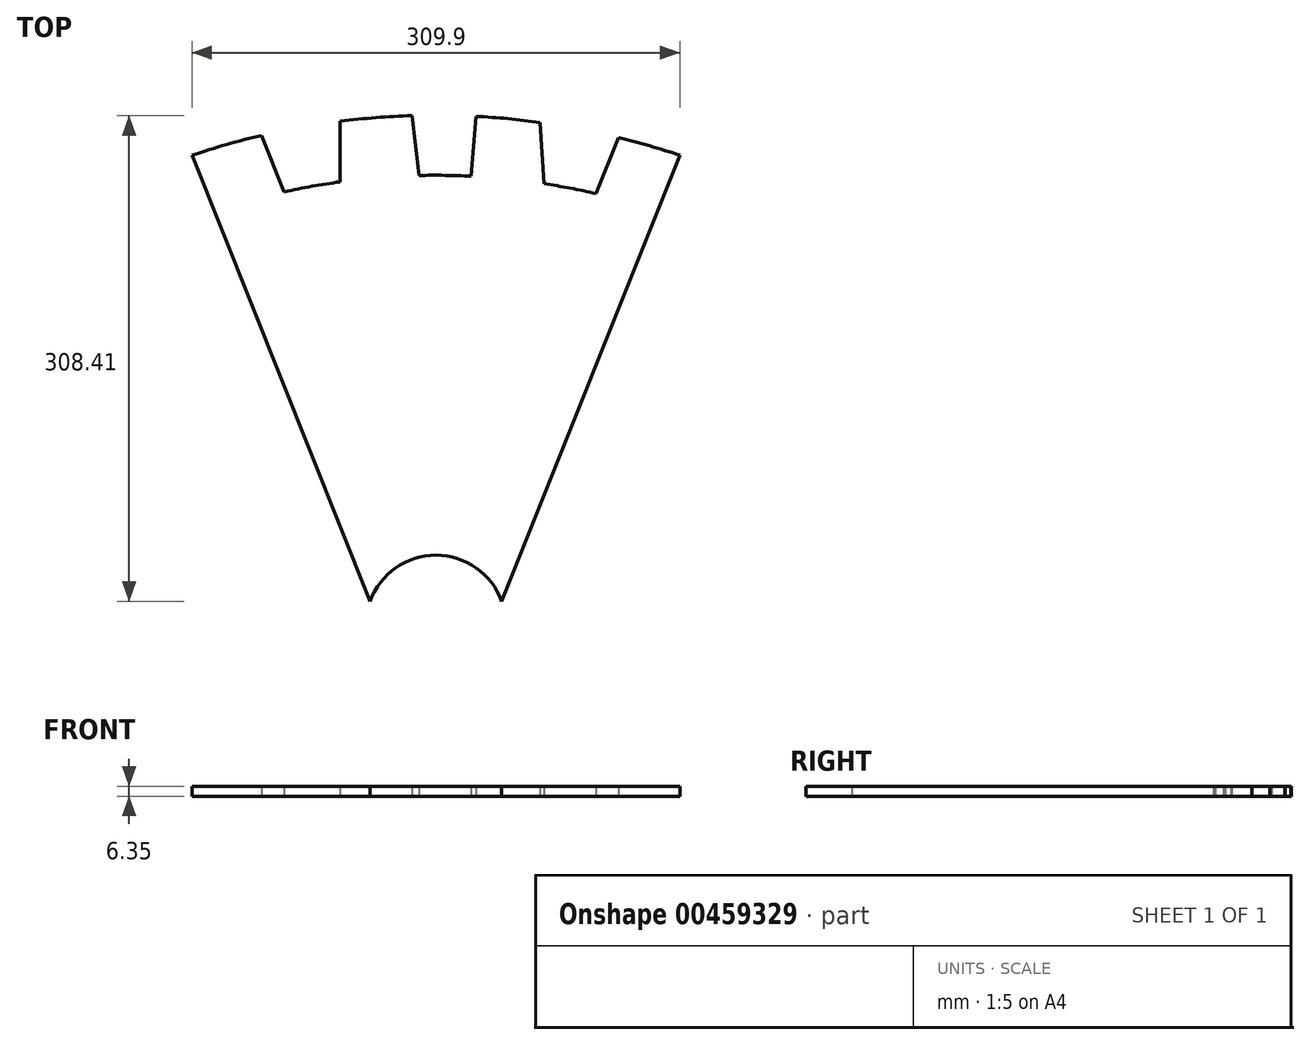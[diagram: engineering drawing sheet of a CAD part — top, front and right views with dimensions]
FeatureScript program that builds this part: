
annotation { "Feature Type Name" : "Feature", "Feature Type Description" : "" }
export const myFeature = defineFeature(function(context is Context, id is Id, definition is map)
    precondition{}
    {
        {
            var Q0;
            Q0=qCreatedBy(makeId("Top.planeOp"),FACE);
            var sketch = newSketch(context, id + "F0", { "sketchPlane" : qUnion([Q0])});
            skCircle(sketch, "E0", {"center": v(0, 0) * mm, "radius": 44.45 * mm});
            skLineSegment(sketch, "E1", {"start": v(0, 0) * mm, "end": v(41.77, 15.2) * mm});
            skLineSegment(sketch, "E2", {"start": v(0, 0) * mm, "end": v(-41.77, 15.2) * mm});
            skLineSegment(sketch, "E3", {"start": v(0, 44.45) * mm, "end": v(0, 323.85) * mm});
            skLineSegment(sketch, "E4", {"start": v(0, 323.85) * mm, "end": v(-165.1, 323.85) * mm});
            skLineSegment(sketch, "E5", {"start": v(0, 323.85) * mm, "end": v(165.1, 323.85) * mm});
            skLineSegment(sketch, "E6", {"start": v(-165.1, 323.85) * mm, "end": v(-41.77, 15.2) * mm});
            skLineSegment(sketch, "E7", {"start": v(165.1, 323.85) * mm, "end": v(41.77, 15.2) * mm});
            skLineSegment(sketch, "E8", {"start": v(-165.1, 323.85) * mm, "end": v(-165.1, 298.45) * mm});
            skLineSegment(sketch, "E9", {"start": v(-165.1, 298.45) * mm, "end": v(-154.95, 298.45) * mm});
            skLineSegment(sketch, "E10", {"start": v(165.1, 323.85) * mm, "end": v(165.1, 298.45) * mm});
            skLineSegment(sketch, "E11", {"start": v(165.1, 298.45) * mm, "end": v(154.95, 298.45) * mm});
            skArc(sketch, "E12", {"start": v(154.95, 298.45) * mm, "mid": v(0, 323.85) * mm, "end": v(-154.95, 298.45) * mm});
            skArc(sketch, "E13.0", {"start": v(140.79, 263.01) * mm, "mid": v(0, 285.75) * mm, "end": v(-140.79, 263.01) * mm});
            skLineSegment(sketch, "E14", {"start": v(115.96, 309.8) * mm, "end": v(101.67, 274.04) * mm});
            skLineSegment(sketch, "E15", {"start": v(66.07, 319.33) * mm, "end": v(66.07, 280.84) * mm});
            skLineSegment(sketch, "E16", {"start": v(25.43, 285.03) * mm, "end": v(25.43, 323.18) * mm});
            skLineSegment(sketch, "E17", {"start": v(-15.21, 285.5) * mm, "end": v(-15.21, 323.61) * mm});
            skLineSegment(sketch, "E18", {"start": v(-55.85, 282.25) * mm, "end": v(-60.8, 320.03) * mm});
            skLineSegment(sketch, "E19", {"start": v(-96.5, 275.22) * mm, "end": v(-110.8, 311.03) * mm});
            skLineSegment(sketch, "E20", {"start": v(-60.8, 320.03) * mm, "end": v(-60.8, 281.6) * mm});
            skLineSegment(sketch, "E21", {"start": v(-15.21, 323.61) * mm, "end": v(-10.8, 285.62) * mm});
            skLineSegment(sketch, "E22", {"start": v(25.43, 323.18) * mm, "end": v(22.26, 285.2) * mm});
            skLineSegment(sketch, "E23", {"start": v(66.07, 319.33) * mm, "end": v(68.55, 280.46) * mm});
            skSolve(sketch);
        }
        {
            var Q0;
            {var subQ5=sQuery(id+"F0.wireOp",EDGE,"E19");Q0=makeQuery(id+"F0.imprint","IMPRINT",FACE,{"disambiguationData":[TD([[makeQuery(id+"F0.imprint","IMPRINT",EDGE,{"derivedFrom":subQ5}),1.0]])]});}
            var Q1;
            {var subQ2=sQuery(id+"F0.wireOp",EDGE,"E3");var subQ5=sQuery(id+"F0.wireOp",EDGE,"E0");var subQ8=makeQuery(id+"F0.imprint","INTERSECT",VERTEX,{"derivedFrom":[subQ5,subQ2]});Q1=makeQuery(id+"F0.imprint","IMPRINT",FACE,{"disambiguationData":[TD([[makeQuery(id+"F0.imprint","IMPRINT",EDGE,{"disambiguationData":[TD([[subQ8,-1.0]])],"derivedFrom":subQ2}),1.0]])]});}
            var Q2;
            {var subQ0=sQuery(id+"F0.wireOp",EDGE,"E18");Q2=makeQuery(id+"F0.imprint","IMPRINT",FACE,{"disambiguationData":[TD([[makeQuery(id+"F0.imprint","IMPRINT",EDGE,{"derivedFrom":subQ0}),1.0]])]});}
            var Q3;
            {var subQ0=sQuery(id+"F0.wireOp",EDGE,"E17");Q3=makeQuery(id+"F0.imprint","IMPRINT",FACE,{"disambiguationData":[TD([[makeQuery(id+"F0.imprint","IMPRINT",EDGE,{"derivedFrom":subQ0}),1.0]])]});}
            var Q4;
            {var subQ0=sQuery(id+"F0.wireOp",EDGE,"E17");Q4=makeQuery(id+"F0.imprint","IMPRINT",FACE,{"disambiguationData":[TD([[makeQuery(id+"F0.imprint","IMPRINT",EDGE,{"derivedFrom":subQ0}),-1.0]])]});}
            var Q5;
            {var subQ0=sQuery(id+"F0.wireOp",EDGE,"E16");Q5=makeQuery(id+"F0.imprint","IMPRINT",FACE,{"disambiguationData":[TD([[makeQuery(id+"F0.imprint","IMPRINT",EDGE,{"derivedFrom":subQ0}),1.0]])]});}
            var Q6;
            {var subQ0=sQuery(id+"F0.wireOp",EDGE,"E15");Q6=makeQuery(id+"F0.imprint","IMPRINT",FACE,{"disambiguationData":[TD([[makeQuery(id+"F0.imprint","IMPRINT",EDGE,{"derivedFrom":subQ0}),-1.0]])]});}
            var Q7;
            {var subQ0=sQuery(id+"F0.wireOp",EDGE,"E15");Q7=makeQuery(id+"F0.imprint","IMPRINT",FACE,{"disambiguationData":[TD([[makeQuery(id+"F0.imprint","IMPRINT",EDGE,{"derivedFrom":subQ0}),1.0]])]});}
            var Q8;
            {var subQ5=sQuery(id+"F0.wireOp",EDGE,"E14");Q8=makeQuery(id+"F0.imprint","IMPRINT",FACE,{"disambiguationData":[TD([[makeQuery(id+"F0.imprint","IMPRINT",EDGE,{"derivedFrom":subQ5}),1.0]])]});}
            var Q9;
            {var subQ4=sQuery(id+"F0.wireOp",EDGE,"E3");var subQ5=sQuery(id+"F0.wireOp",EDGE,"E0");var subQ6=makeQuery(id+"F0.imprint","INTERSECT",VERTEX,{"derivedFrom":[subQ5,subQ4]});Q9=makeQuery(id+"F0.imprint","IMPRINT",FACE,{"disambiguationData":[TD([[makeQuery(id+"F0.imprint","IMPRINT",EDGE,{"disambiguationData":[TD([[subQ6,-1.0]])],"derivedFrom":subQ4}),-1.0]])]});}
            extrude(context, id + "F1", {"entities" : qUnion([Q0, Q1, Q2, Q3, Q4, Q5, Q6, Q7, Q8, Q9]), "depth" : 6.35 * mm, "offsetDistance" : 25.4 * mm});
        }
    });
